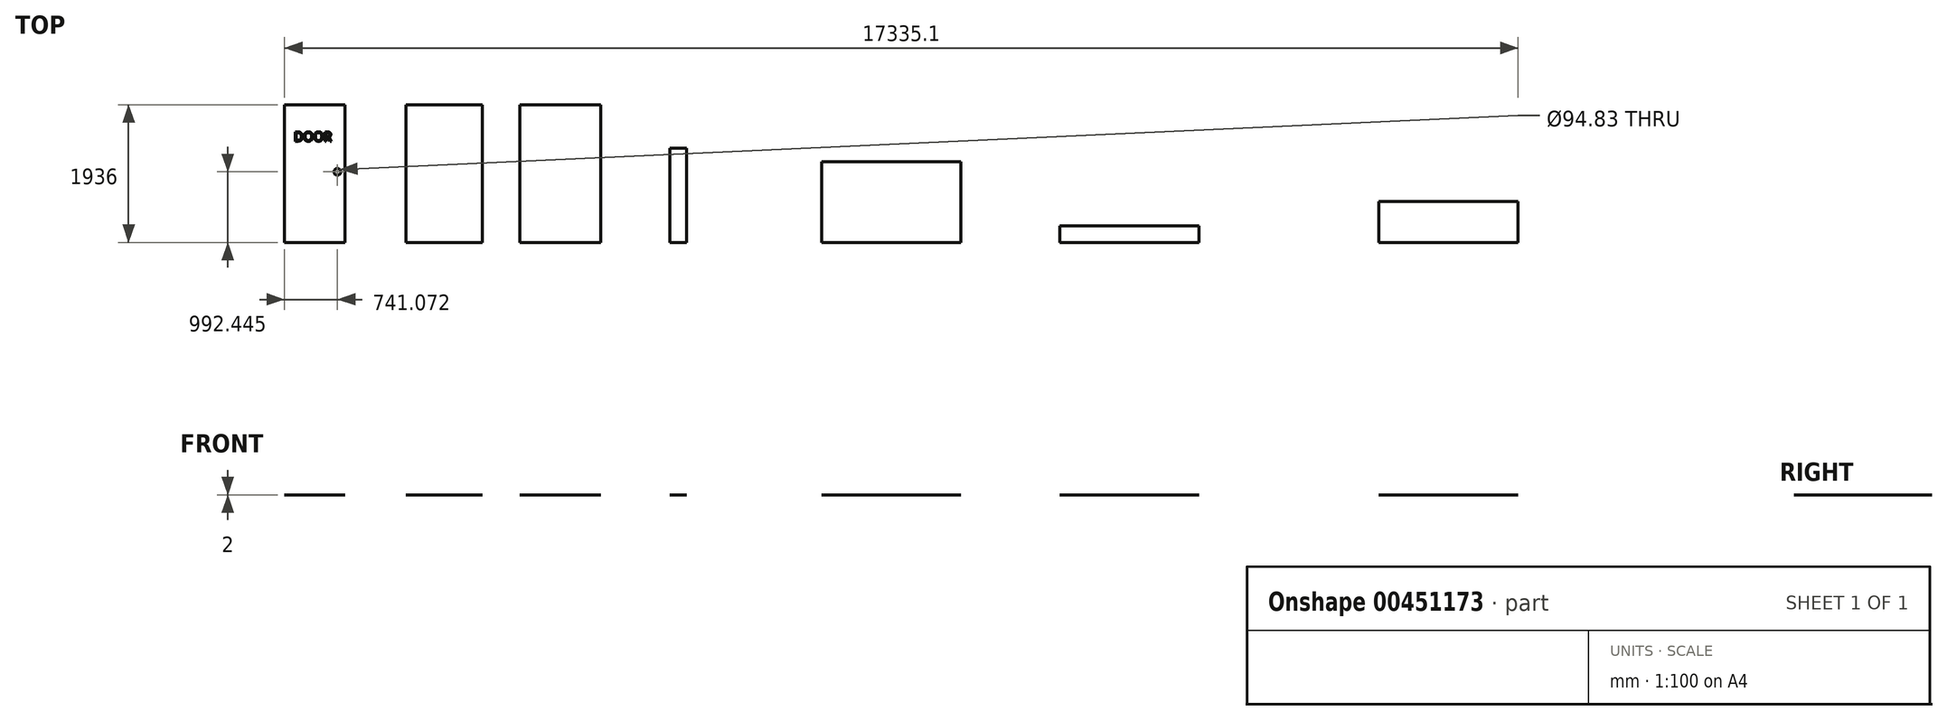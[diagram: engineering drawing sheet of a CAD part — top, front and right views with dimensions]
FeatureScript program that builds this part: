
annotation { "Feature Type Name" : "Feature", "Feature Type Description" : "" }
export const myFeature = defineFeature(function(context is Context, id is Id, definition is map)
    precondition{}
    {
        {
            var Q0;
            Q0=qCreatedBy(makeId("Top.planeOp"),FACE);
            var sketch = newSketch(context, id + "F0", { "sketchPlane" : qUnion([Q0])});
            skLineSegment(sketch, "E0.bottom", {"start": v(-850, 1936) * mm, "end": v(0, 1936) * mm});
            skLineSegment(sketch, "E0.top", {"start": v(-850, 0) * mm, "end": v(0, 0) * mm});
            skLineSegment(sketch, "E0.left", {"start": v(-850, 1936) * mm, "end": v(-850, 0) * mm});
            skLineSegment(sketch, "E0.right", {"start": v(0, 1936) * mm, "end": v(0, 0) * mm});
            skCircle(sketch, "E1", {"center": v(-108.93, 992.45) * mm, "radius": 47.42 * mm});
            skLineSegment(sketch, "E2.bottom", {"start": v(853.98, 0) * mm, "end": v(1927.98, 0) * mm});
            skLineSegment(sketch, "E2.top", {"start": v(853.98, 1936) * mm, "end": v(1927.98, 1936) * mm});
            skLineSegment(sketch, "E2.left", {"start": v(853.98, 0) * mm, "end": v(853.98, 1936) * mm});
            skLineSegment(sketch, "E2.right", {"start": v(1927.98, 0) * mm, "end": v(1927.98, 1936) * mm});
            skLineSegment(sketch, "E3.bottom", {"start": v(2453.88, 0) * mm, "end": v(3589.88, 0) * mm});
            skLineSegment(sketch, "E3.top", {"start": v(2453.88, 1936) * mm, "end": v(3589.88, 1936) * mm});
            skLineSegment(sketch, "E3.left", {"start": v(2453.88, 0) * mm, "end": v(2453.88, 1936) * mm});
            skLineSegment(sketch, "E3.right", {"start": v(3589.88, 0) * mm, "end": v(3589.88, 1936) * mm});
            skLineSegment(sketch, "E4.bottom", {"start": v(4562.83, 0) * mm, "end": v(4798.83, 0) * mm});
            skLineSegment(sketch, "E4.top", {"start": v(4562.83, 1328) * mm, "end": v(4798.83, 1328) * mm});
            skLineSegment(sketch, "E4.left", {"start": v(4562.83, 0) * mm, "end": v(4562.83, 1328) * mm});
            skLineSegment(sketch, "E4.right", {"start": v(4798.83, 0) * mm, "end": v(4798.83, 1328) * mm});
            skLineSegment(sketch, "E5.bottom", {"start": v(6695.86, 0) * mm, "end": v(8651.86, 0) * mm});
            skLineSegment(sketch, "E5.top", {"start": v(6695.86, 1136) * mm, "end": v(8651.86, 1136) * mm});
            skLineSegment(sketch, "E5.left", {"start": v(6695.86, 0) * mm, "end": v(6695.86, 1136) * mm});
            skLineSegment(sketch, "E5.right", {"start": v(8651.86, 0) * mm, "end": v(8651.86, 1136) * mm});
            skLineSegment(sketch, "E6.bottom", {"start": v(10041.1, 0) * mm, "end": v(11997.1, 0) * mm});
            skLineSegment(sketch, "E6.top", {"start": v(10041.1, 236) * mm, "end": v(11997.1, 236) * mm});
            skLineSegment(sketch, "E6.left", {"start": v(10041.1, 0) * mm, "end": v(10041.1, 236) * mm});
            skLineSegment(sketch, "E6.right", {"start": v(11997.1, 0) * mm, "end": v(11997.1, 236) * mm});
            skLineSegment(sketch, "E7.bottom", {"start": v(14529.12, 0) * mm, "end": v(16485.12, 0) * mm});
            skLineSegment(sketch, "E7.top", {"start": v(14529.12, 576) * mm, "end": v(16485.12, 576) * mm});
            skLineSegment(sketch, "E7.left", {"start": v(14529.12, 0) * mm, "end": v(14529.12, 576) * mm});
            skLineSegment(sketch, "E7.right", {"start": v(16485.12, 0) * mm, "end": v(16485.12, 576) * mm});
            skSolve(sketch);
        }
        {
            var Q0;
            Q0 = qSketchRegion(id + "F0", true);
            extrude(context, id + "F1", {"entities" : qUnion([Q0]), "depth" : 2 * mm, "offsetDistance" : 25 * mm});
        }
        {
            var Q0;
            Q0=makeQuery(id+"F1.opExtrude","CAP_FACE",FACE,{"disambiguationData":[OSD([sQuery(id+"F0.wireOp",EDGE,"E0.bottom"),sQuery(id+"F0.wireOp",EDGE,"E0.top"),sQuery(id+"F0.wireOp",EDGE,"E0.left"),sQuery(id+"F0.wireOp",EDGE,"E0.right"),sQuery(id+"F0.wireOp",EDGE,"E1")])],"isStart":false});
            var sketch = newSketch(context, id + "F2", { "sketchPlane" : qUnion([Q0])});
            skText(sketch, "E8", { "text": "DOOR", "fontName": "OpenSans-Regular.ttf"});
            const initialGuessF2  = {"E8": [-0.72176, 1.42296, 1, 0, 0.13215]};
            skSetInitialGuess(sketch, initialGuessF2);
            skSolve(sketch);
        }
        {
            var Q0;
            Q0 = qSketchRegion(id + "F2", true);
            extrude(context, id + "F3", {"entities" : qUnion([Q0]), "operationType" : NewBodyOperationType.REMOVE, "oppositeDirection" : true, "depth" : 1 * mm, "offsetDistance" : 25 * mm});
        }
    });
